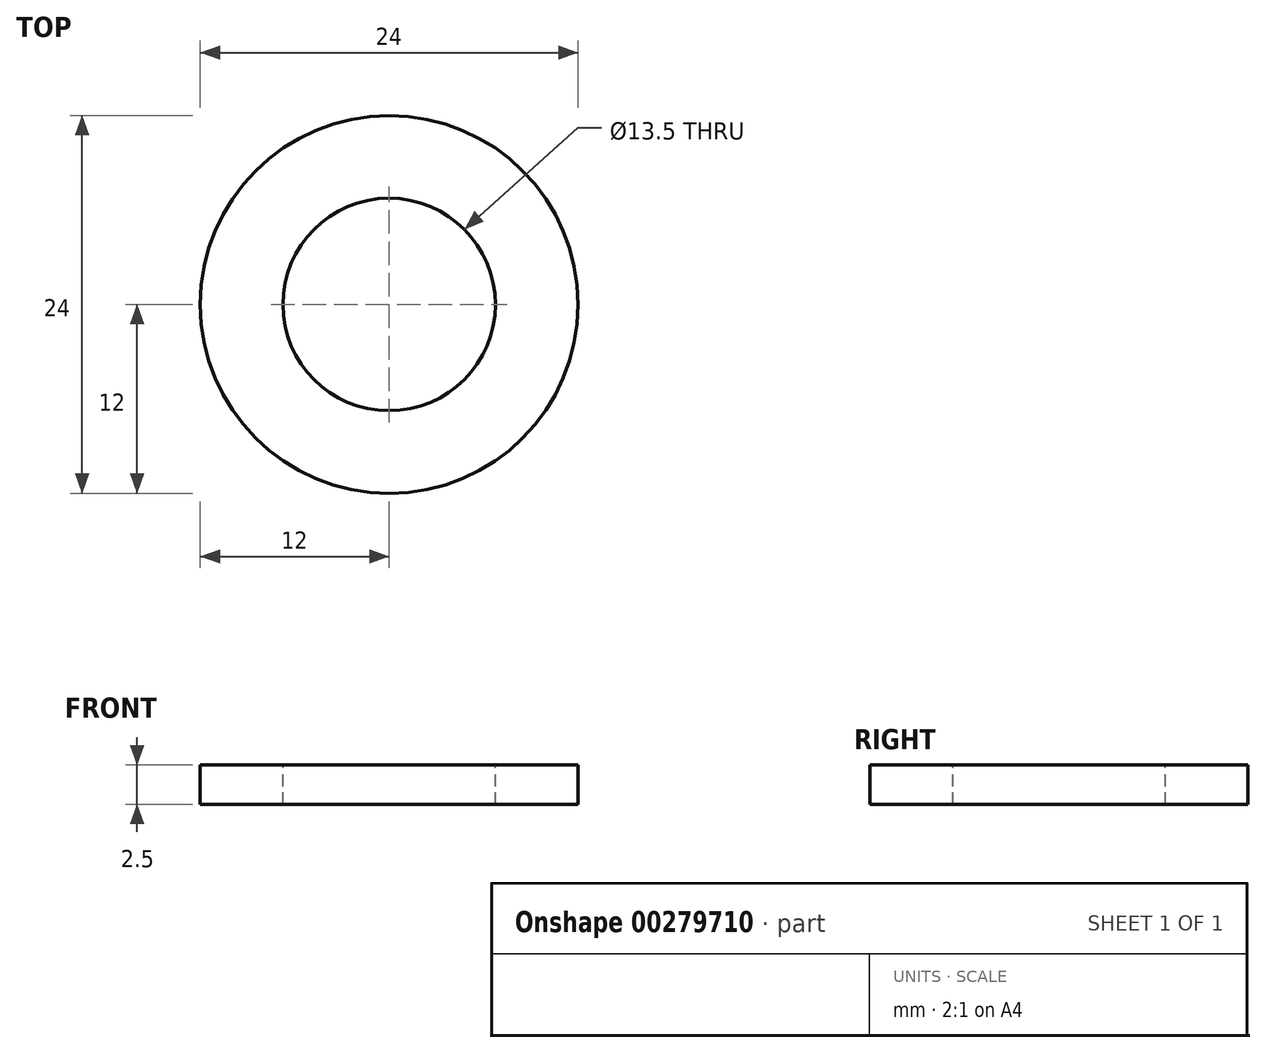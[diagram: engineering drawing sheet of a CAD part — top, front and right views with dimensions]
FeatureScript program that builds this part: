
annotation { "Feature Type Name" : "Feature", "Feature Type Description" : "" }
export const myFeature = defineFeature(function(context is Context, id is Id, definition is map)
    precondition{}
    {
        {
            var Q0;
            Q0=qCreatedBy(makeId("Front.planeOp"),FACE);
            var sketch = newSketch(context, id + "F0", { "sketchPlane" : qUnion([Q0])});
            skLineSegment(sketch, "E0", {"start": v(0, 3.9) * mm, "end": v(0, -4.8) * mm, "construction": true});
            skLineSegment(sketch, "E1.bottom", {"start": v(-12, 0) * mm, "end": v(-6.75, 0) * mm});
            skLineSegment(sketch, "E1.top", {"start": v(-12, 2.5) * mm, "end": v(-6.75, 2.5) * mm});
            skLineSegment(sketch, "E1.left", {"start": v(-12, 0) * mm, "end": v(-12, 2.5) * mm});
            skLineSegment(sketch, "E1.right", {"start": v(-6.75, 0) * mm, "end": v(-6.75, 2.5) * mm});
            skSolve(sketch);
        }
        {
            var Q0;
            Q0=makeQuery(id+"F0.imprint","IMPRINT",FACE,{"disambiguationData":[TD([[makeQuery(id+"F0.imprint","IMPRINT",EDGE,{"derivedFrom":sQuery(id+"F0.wireOp",EDGE,"E1.bottom")}),1.0]])]});
            var Q1;
            Q1=sQuery(id+"F0.wireOp",EDGE,"E0");
            revolve(context, id + "F1", {"entities" : qUnion([Q0]), "axis" : qUnion([Q1]), "revolveType" : RevolveType.FULL});
        }
    });
